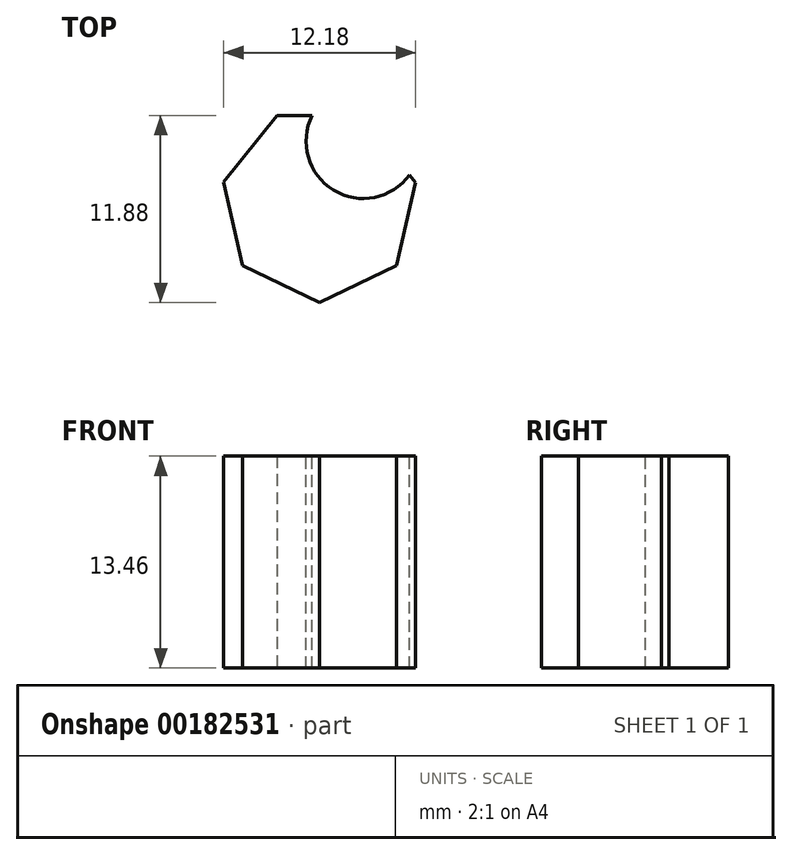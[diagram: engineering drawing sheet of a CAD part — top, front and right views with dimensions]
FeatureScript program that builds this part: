
annotation { "Feature Type Name" : "Feature", "Feature Type Description" : "" }
export const myFeature = defineFeature(function(context is Context, id is Id, definition is map)
    precondition{}
    {
        {
            var Q0;
            Q0=qCreatedBy(makeId("Top.planeOp"),FACE);
            var sketch = newSketch(context, id + "F0", { "sketchPlane" : qUnion([Q0])});
            skCircle(sketch, "E0.cCircle", {"center": v(2.45, 3.12) * mm, "radius": 5.63 * mm, "construction": true});
            skLineSegment(sketch, "E0.0", {"start": v(2.44, -3.13) * mm, "end": v(-2.44, -0.77) * mm});
            skLineSegment(sketch, "E0.1", {"start": v(-2.44, -0.77) * mm, "end": v(-3.64, 4.52) * mm});
            skLineSegment(sketch, "E0.2", {"start": v(-3.64, 4.52) * mm, "end": v(-0.25, 8.75) * mm});
            skLineSegment(sketch, "E0.3", {"start": v(-0.25, 8.75) * mm, "end": v(5.17, 8.74) * mm});
            skLineSegment(sketch, "E0.4", {"start": v(5.17, 8.74) * mm, "end": v(8.54, 4.5) * mm});
            skLineSegment(sketch, "E0.5", {"start": v(8.54, 4.5) * mm, "end": v(7.33, -0.79) * mm});
            skLineSegment(sketch, "E0.6", {"start": v(7.33, -0.79) * mm, "end": v(2.44, -3.13) * mm});
            skPoint(sketch, "E0.0.midPoint", {"position": v(0, -1.95) * mm});
            skSolve(sketch);
        }
        {
            var Q0;
            Q0 = qSketchRegion(id + "F0", true);
            extrude(context, id + "F1", {"entities" : qUnion([Q0]), "depth" : 13.46 * mm});
        }
        {
            var Q0;
            Q0=makeQuery(id+"F1.opExtrude","CAP_FACE",FACE,{"disambiguationData":[OSD([sQuery(id+"F0.wireOp",EDGE,"E0.0"),sQuery(id+"F0.wireOp",EDGE,"E0.1"),sQuery(id+"F0.wireOp",EDGE,"E0.2"),sQuery(id+"F0.wireOp",EDGE,"E0.3"),sQuery(id+"F0.wireOp",EDGE,"E0.4"),sQuery(id+"F0.wireOp",EDGE,"E0.5"),sQuery(id+"F0.wireOp",EDGE,"E0.6")])],"isStart":false});
            var sketch = newSketch(context, id + "F2", { "sketchPlane" : qUnion([Q0])});
            skCircle(sketch, "E1", {"center": v(5.22, 7.11) * mm, "radius": 3.63 * mm});
            skSolve(sketch);
        }
        {
            var Q0;
            Q0=makeQuery(id+"F2.imprint","IMPRINT",FACE,{"disambiguationData":[TD([[makeQuery(id+"F2.imprint","IMPRINT",EDGE,{"derivedFrom":sQuery(id+"F2.wireOp",EDGE,"E1")}),1.0]])]});
            extrude(context, id + "F3", {"entities" : qUnion([Q0]), "operationType" : NewBodyOperationType.REMOVE, "oppositeDirection" : true, "depth" : 25.4 * mm});
        }
    });
